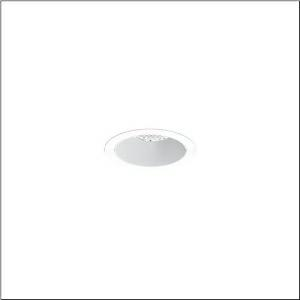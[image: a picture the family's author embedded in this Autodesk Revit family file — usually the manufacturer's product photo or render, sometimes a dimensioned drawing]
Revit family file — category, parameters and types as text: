
# Revit family: lunis_21_m_51db18tc91c
name_source: partatom
category: Lighting Fixtures
units: mm (PartAtom-declared; Revit-internal decimal feet)

## family parameters
Cut with Voids When Loaded = No
Host = Face
Light Source = No
Part Type = Normal
Room Calculation Point = No
Round Connector Dimension = Use Diameter
Shared = No

## types (1)
- --- (1 x LED 3000 K ... 6500 K, 3910 lm, 26 W, 4000K)
    Apparent Load = 26 VA
    CIE Flux Codes = 86 95 99 100 100
    Color Rendering = 80
    Color Temperature = 4000K
    Default Elevation = 1800 mm
    Description = Lunis 21 M, downlight, light control with lens, of PMMA, anti glare with reflector, of aluminium, light emission: direct distribution, LED rated luminous flux: 3.910lm, light colour: 8tw, with terminal, 5-pole, mains connection: 220..240V, AC/DC, 0/50..60Hz, housing, round, of diecast aluminium, traffic white (RAL 9016), diameter: 115mm, clamping range: 1..40mm, protection rating (complete): IP20, protection rating (on room side): IP54, insulation class (complete): insulation class II (safety insulation), certification: CE, impact resistance: IK03, packaging unit: 1 piece
    Height = 0 mm  [stored 0 ft]
    Lamp = 1 x LED 3000 K ... 6500 K
    Lamp Light Flux = 3910 lm
    Lamp Power = 26 W
    Lamp count = 1
    Length = 115 mm
    Luminous efficacy = 150 lm/W
    Manufacturer = Siteco
    ModVariant = No
    Model = 51DB18TC91C
    Mounting Place = Ceiling
    Mounting Type = Recessed
    Number of Poles = 1
    OnlyDefault = Yes
    Power Factor = 1
    Product Name = Lunis 21 M
    Product group = downlight
    ProductGroupID = 401
    Protection Class = Protection class II
    Protection Degree = IP 20
    RLX_Detail_Level = 1
    RLX_Emergency_Light_Flux = 0 lm
    RLX_Emergency_Type = 0
    RLX_Emergency_Type_DB = No
    RlxData = <blob elided: 10541 chars, md5=92a65b8e>
    Socket = socket
    Standby Power = 0 W
    System Light Flux = 3910 lm
    System Power = 26 W
    Type Comments = individual setting: CCT=4000K, colour temperature 4000K, luminous flux: 100 % | (ON | ON | OFF | OFF) | 700 mA
    Type Image = l_1290852.jpg
    URL = http://relux.com
    VarID = @adj_035367
    Voltage = 0 V
    Weight = 0.00 kg
    Width = 0 mm  [stored 0 ft]

note: [stored X ft] marks values corroborated as IEEE doubles in the binary element streams (Revit-internal decimal feet)

## geometry (parser evidence)
native form markers: Sweep x11
no freeform markers — native parametric forms only
